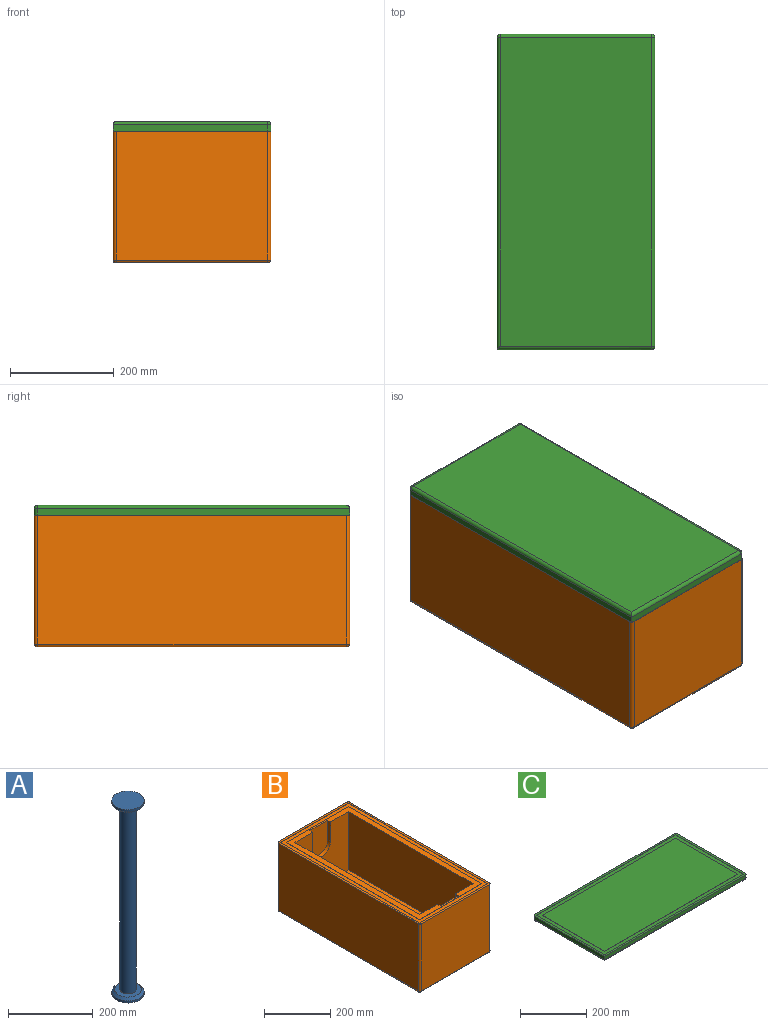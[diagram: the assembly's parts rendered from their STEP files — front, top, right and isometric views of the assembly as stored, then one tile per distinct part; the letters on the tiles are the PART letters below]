
ASSEMBLY  parts=3 mates=2
PART A: 9 faces, bbox 76.2x76.2x558.8 mm
  f0: cylinder r=38.1mm len=76.2mm, axis (0,0,-1), area 1520.1mm2, adj f2,f8
  f1: plane 63.5x63.5mm, normal (0,0,1), area 2026.8mm2, adj f3,f8
  f2: plane 76.2x76.2mm, normal (0,0,-1), area 4560.4mm2, adj f0
  f3: cylinder r=19.05mm len=533.4mm, axis (0,0,-1), area 63845.1mm2, adj f1,f6
  f4: cylinder r=38.1mm len=76.2mm, axis (0,0,-1), area 1520.1mm2, adj f5,f7
  f5: plane 76.2x76.2mm, normal (0,0,1), area 4560.4mm2, adj f4
  f6: plane 63.5x63.5mm, normal (0,0,-1), area 2026.8mm2, adj f3,f7
  f7: cone r=38.1mm half-angle=45deg, axis (0,0,1), area 1970.6mm2, adj f4,f6
  f8: cone r=31.75mm half-angle=45deg, axis (0,0,-1), area 1970.6mm2, adj f0,f1
PART B: 41 faces, bbox 304.8x609.6x254 mm
  f0: plane 571.5x266.7mm, normal (0,0,1), area 28548.3mm2, adj f1,f2,f3,f4,f6,f8,f9,f10
  f1: plane 228.6x215.9mm, normal (0,1,0), area 41567.6mm2, adj f0,f2,f4,f5,f10,f11,f12
  f2: plane 533.4x215.9mm, normal (-1,0,0), area 115161.1mm2, adj f0,f1,f3,f5
  f3: plane 228.6x215.9mm, normal (0,-1,0), area 41567.6mm2, adj f0,f2,f4,f5,f6,f7,f8
  f4: plane 533.4x215.9mm, normal (1,0,0), area 115161.1mm2, adj f0,f1,f3,f5
  f5: plane 533.4x228.6mm, normal (0,0,1), area 121935.2mm2, adj f1,f2,f3,f4
  f6: plane 72.27x12.7mm, normal (1,0,0), area 917.8mm2, adj f0,f3,f7,f9
  f7: cylinder r=38.1mm len=76.2mm, axis (0,-1,0), area 1520.1mm2, adj f3,f6,f8,f9
  f8: plane 72.27x12.7mm, normal (-1,0,0), area 917.8mm2, adj f0,f3,f7,f9
  f9: plane 110.37x76.2mm, normal (0,-1,0), area 7787.1mm2, adj f0,f6,f7,f8
  f10: plane 72.27x12.7mm, normal (-1,0,0), area 917.8mm2, adj f0,f1,f11,f13
  f11: cylinder r=38.1mm len=76.2mm, axis (0,1,0), area 1520.1mm2, adj f1,f10,f12,f13
  f12: plane 72.27x12.7mm, normal (1,0,0), area 917.8mm2, adj f0,f1,f11,f13
  f13: plane 110.37x76.2mm, normal (0,1,0), area 7787.1mm2, adj f0,f10,f11,f12
  f14: plane 292.1x0.8mm, normal (0,-1,0), area 233.7mm2, adj f15,f21,f22,f28
  f15: plane 596.9x0.8mm, normal (1,0,0), area 477.6mm2, adj f14,f16,f22,f28
  f16: plane 292.1x0.8mm, normal (0,1,0), area 233.7mm2, adj f15,f21,f22,f28
  f17: plane 571.5x0.8mm, normal (-1,0,0), area 457.3mm2, adj f0,f18,f20,f22
  f18: plane 266.7x0.8mm, normal (0,1,0), area 213.4mm2, adj f0,f17,f19,f22
  f19: plane 571.5x0.8mm, normal (1,0,0), area 457.3mm2, adj f0,f18,f20,f22
  f20: plane 266.7x0.8mm, normal (0,-1,0), area 213.4mm2, adj f0,f17,f19,f22
  f21: plane 596.9x0.8mm, normal (-1,0,0), area 477.6mm2, adj f14,f16,f22,f28
  f22: plane 596.9x292.1mm, normal (0,0,1), area 21935.4mm2, adj f14,f15,f16,f17,f18,f19,f20,f21
  f23: plane 599.44x294.64mm, normal (0,0,-1), area 176617.6mm2, adj f33,f34,f35,f36,f37,f38,f39,f40
  f24: plane 292.1x248.92mm, normal (0,-1,0), area 72709.5mm2, adj f28,f31,f32,f37
  f25: plane 596.9x248.92mm, normal (-1,0,0), area 148580.3mm2, adj f28,f30,f31,f40
  f26: plane 292.1x248.92mm, normal (0,1,0), area 72709.5mm2, adj f28,f29,f30,f36
  f27: plane 596.9x248.92mm, normal (1,0,0), area 148580.3mm2, adj f28,f29,f32,f33
  f28: plane 609.6x304.8mm, normal (0,0,1), area 11417mm2, adj f14,f15,f16,f21,f24,f25,f26,f27
  f29: cylinder r=6.35mm len=248.92mm, axis (0,0,1), area 2482.9mm2, adj f26,f27,f28,f34
  f30: cylinder r=6.35mm len=248.92mm, axis (0,0,-1), area 2482.9mm2, adj f25,f26,f28,f38
  f31: cylinder r=6.35mm len=248.92mm, axis (0,0,1), area 2482.9mm2, adj f24,f25,f28,f39
  f32: cylinder r=6.35mm len=248.92mm, axis (0,0,-1), area 2482.9mm2, adj f24,f27,f28,f35
  f33: cylinder r=5.08mm len=596.9mm, axis (0,1,0), area 4763.1mm2, adj f23,f27,f34,f35
  f34: torus R=1.27mm, axis (0,0,1), area 56.5mm2, adj f23,f29,f33,f36
  f35: torus R=1.27mm, axis (0,0,1), area 56.5mm2, adj f23,f32,f33,f37
  f36: cylinder r=5.08mm len=292.1mm, axis (-1,0,0), area 2330.9mm2, adj f23,f26,f34,f38
  f37: cylinder r=5.08mm len=292.1mm, axis (1,0,0), area 2330.9mm2, adj f23,f24,f35,f39
  f38: torus R=1.27mm, axis (0,0,1), area 56.5mm2, adj f23,f30,f36,f40
  f39: torus R=1.27mm, axis (0,0,1), area 56.5mm2, adj f23,f31,f37,f40
  f40: cylinder r=5.08mm len=596.9mm, axis (0,-1,0), area 4763.1mm2, adj f23,f25,f38,f39
PART C: 26 faces, bbox 609.6x304.8x19.1 mm
  f0: plane 292.1x12.7mm, normal (1,0,0), area 3709.7mm2, adj f4,f19,f23,f25
  f1: plane 596.9x12.7mm, normal (0,1,0), area 7580.6mm2, adj f4,f16,f22,f25
  f2: plane 298.45x12.7mm, normal (-1,0,0), area 3790.3mm2, adj f3,f4,f16,f17
  f3: plane 603.25x12.7mm, normal (0,-1,0), area 7661.3mm2, adj f2,f4,f18,f19
  f4: plane 609.6x304.8mm, normal (0,0,1), area 11425.6mm2, adj f0,f1,f2,f3,f6,f7,f8,f13
  f5: plane 596.9x292.1mm, normal (0,0,-1), area 174354.5mm2, adj f17,f18,f22,f23
  f6: plane 596.9x0.81mm, normal (0,-1,0), area 485.2mm2, adj f4,f7,f13,f14
  f7: plane 292.1x0.81mm, normal (1,0,0), area 237.4mm2, adj f4,f6,f8,f14
  f8: plane 596.9x0.81mm, normal (0,1,0), area 485.2mm2, adj f4,f7,f13,f14
  f9: plane 266.7x0.81mm, normal (-1,0,0), area 216.8mm2, adj f10,f12,f14,f15
  f10: plane 571.5x0.81mm, normal (0,1,0), area 464.5mm2, adj f9,f11,f14,f15
  f11: plane 266.7x0.81mm, normal (1,0,0), area 216.8mm2, adj f10,f12,f14,f15
  f12: plane 571.5x0.81mm, normal (0,-1,0), area 464.5mm2, adj f9,f11,f14,f15
  f13: plane 292.1x0.81mm, normal (-1,0,0), area 237.4mm2, adj f4,f6,f8,f14
  f14: plane 596.9x292.1mm, normal (0,0,1), area 21935.4mm2, adj f6,f7,f8,f9,f10,f11,f12,f13
  f15: plane 571.5x266.7mm, normal (0,0,1), area 152419mm2, adj f9,f10,f11,f12
  f16: cylinder r=6.35mm len=12.7mm, axis (0,0,-1), area 126.7mm2, adj f1,f2,f4,f20
  f17: cylinder r=6.35mm len=298.45mm, axis (0,-1,0), area 2953.9mm2, adj f2,f5,f18,f20
  f18: cylinder r=6.35mm len=603.25mm, axis (1,0,0), area 5994.1mm2, adj f3,f5,f17,f21
  f19: cylinder r=6.35mm len=12.7mm, axis (0,0,-1), area 126.7mm2, adj f0,f3,f4,f21
  f20: sphere r=6.35mm, area 63.3mm2, adj f16,f17,f22
  f21: sphere r=6.35mm, area 63.3mm2, adj f18,f19,f23
  f22: cylinder r=6.35mm len=596.9mm, axis (-1,0,0), area 5953.8mm2, adj f1,f5,f20,f24
  f23: cylinder r=6.35mm len=292.1mm, axis (0,1,0), area 2913.6mm2, adj f0,f5,f21,f24
  f24: sphere r=6.35mm, area 63.3mm2, adj f22,f23,f25
  f25: cylinder r=6.35mm len=12.7mm, axis (0,0,1), area 126.7mm2, adj f0,f1,f4,f24
PLACE A rot(axis=(-1,0,0),90deg) t=(-11.55,-141.95,118.5)mm
PLACE B t=(-11.55,137.45,-63.23)mm fixed
PLACE C rot(axis=(0.71,0.71,0),180deg) t=(-11.43,137.68,209.82)mm
MATE revolute A.f4 <-> B.f7  axis (0,1,0) through (-11.55,416.85,118.5)mm
MATE fastened C.f15 <-> B.f0  axis (0,0,-1) through (-11.55,137.45,190.77)mm
